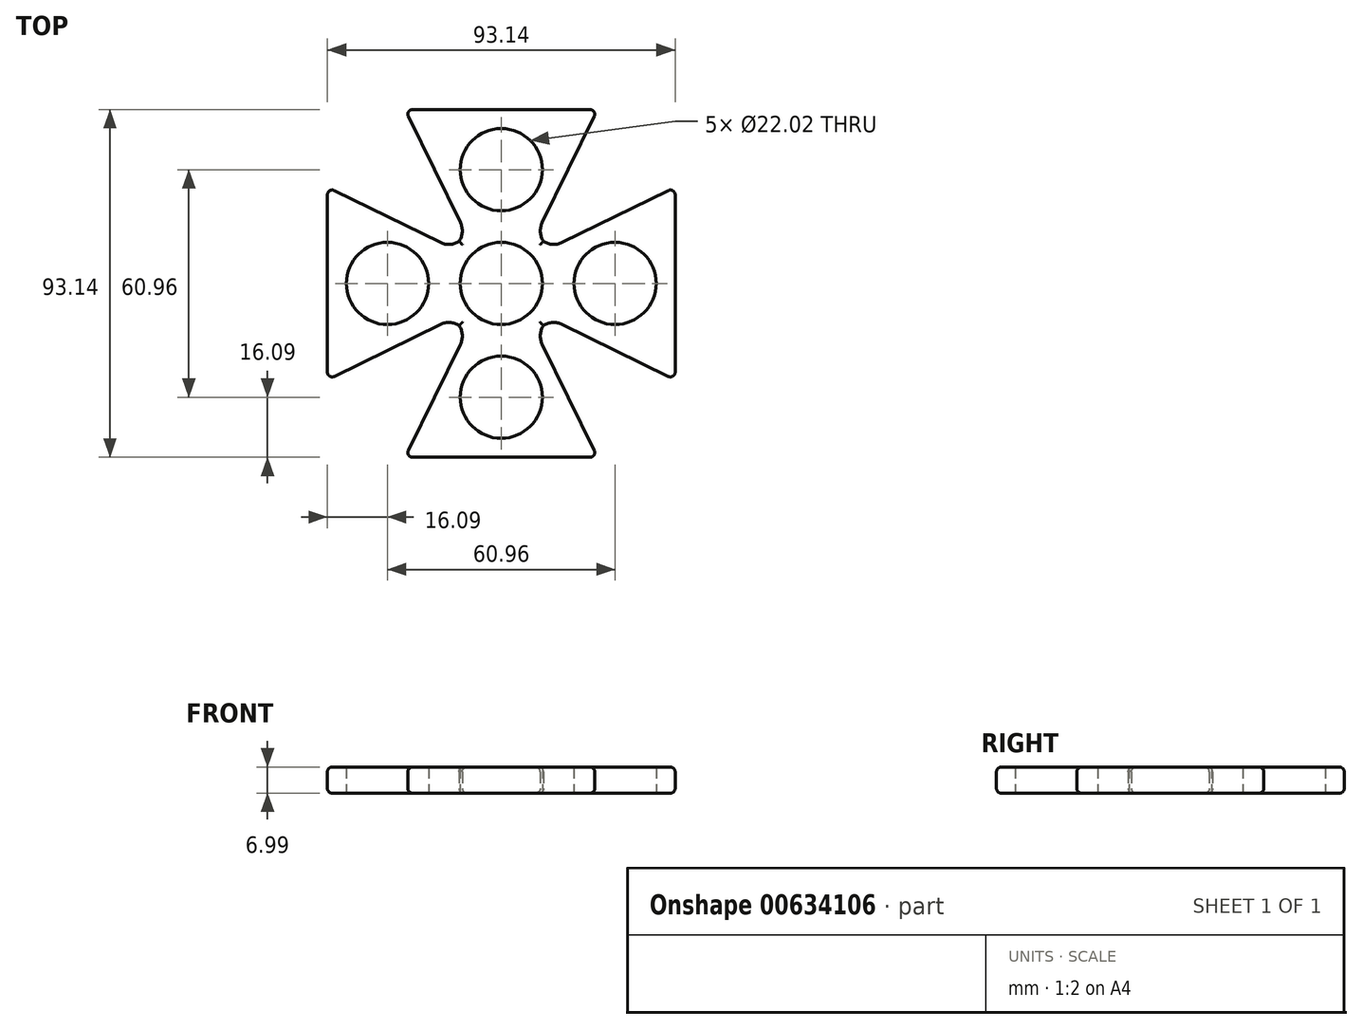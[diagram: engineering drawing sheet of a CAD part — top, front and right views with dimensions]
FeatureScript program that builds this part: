
annotation { "Feature Type Name" : "Feature", "Feature Type Description" : "" }
export const myFeature = defineFeature(function(context is Context, id is Id, definition is map)
    precondition{}
    {
        {
            var Q0;
            Q0=qCreatedBy(makeId("Top.planeOp"),FACE);
            var sketch = newSketch(context, id + "F0", { "sketchPlane" : qUnion([Q0])});
            skCircle(sketch, "E0", {"center": v(0, 0) * mm, "radius": 11.01 * mm});
            skLineSegment(sketch, "E1", {"start": v(0, 0) * mm, "end": v(0, 30.48) * mm});
            skCircle(sketch, "E2", {"center": v(0, 30.48) * mm, "radius": 11.01 * mm});
            skCircle(sketch, "E3", {"center": v(0, 0) * mm, "radius": 15.88 * mm});
            skLineSegment(sketch, "E4", {"start": v(-9.3, 12.87) * mm, "end": v(-25.8, 46.57) * mm});
            skLineSegment(sketch, "E5", {"start": v(-25.8, 46.57) * mm, "end": v(25.8, 46.57) * mm});
            skLineSegment(sketch, "E6", {"start": v(25.8, 46.57) * mm, "end": v(9.3, 12.87) * mm});
            skLineSegment(sketch, "E7.1.0", {"start": v(-46.57, -25.8) * mm, "end": v(-46.57, 25.8) * mm});
            skLineSegment(sketch, "E7.1.1", {"start": v(-12.87, -9.3) * mm, "end": v(-46.57, -25.8) * mm});
            skCircle(sketch, "E7.1.2", {"center": v(-30.48, 0) * mm, "radius": 11.01 * mm});
            skLineSegment(sketch, "E7.1.3", {"start": v(-46.57, 25.8) * mm, "end": v(-12.87, 9.3) * mm});
            skLineSegment(sketch, "E7.1.4", {"start": v(0, 0) * mm, "end": v(-30.48, 0) * mm});
            skLineSegment(sketch, "E7.2.0", {"start": v(25.8, -46.57) * mm, "end": v(-25.8, -46.57) * mm});
            skLineSegment(sketch, "E7.2.1", {"start": v(9.3, -12.87) * mm, "end": v(25.8, -46.57) * mm});
            skCircle(sketch, "E7.2.2", {"center": v(0, -30.48) * mm, "radius": 11.01 * mm});
            skLineSegment(sketch, "E7.2.3", {"start": v(-25.8, -46.57) * mm, "end": v(-9.3, -12.87) * mm});
            skLineSegment(sketch, "E7.2.4", {"start": v(0, 0) * mm, "end": v(0, -30.48) * mm});
            skLineSegment(sketch, "E7.3.0", {"start": v(46.57, 25.8) * mm, "end": v(46.57, -25.8) * mm});
            skLineSegment(sketch, "E7.3.1", {"start": v(12.87, 9.3) * mm, "end": v(46.57, 25.8) * mm});
            skCircle(sketch, "E7.3.2", {"center": v(30.48, 0) * mm, "radius": 11.01 * mm});
            skLineSegment(sketch, "E7.3.3", {"start": v(46.57, -25.8) * mm, "end": v(12.87, -9.3) * mm});
            skLineSegment(sketch, "E7.3.4", {"start": v(0, 0) * mm, "end": v(30.48, 0) * mm});
            skPoint(sketch, "E8", {"position": v(0, 46.57) * mm});
            skLineSegment(sketch, "E9", {"start": v(0, 30.48) * mm, "end": v(0, 46.57) * mm});
            skLineSegment(sketch, "E10", {"start": v(0, 0) * mm, "end": v(-11.23, -11.23) * mm});
            skSolve(sketch);
        }
        {
            var Q0;
            Q0 = qSketchRegion(id + "F0", true);
            extrude(context, id + "F1", {"entities" : qUnion([Q0]), "depth" : 7 * mm, "offsetDistance" : 25.4 * mm});
        }
        {
            var Q0;
            Q0=makeQuery(id+"F1.opExtrude","SWEPT_EDGE",EDGE,{"disambiguationData":[OSD([sQuery(id+"F0.wireOp",EDGE,"E4"),sQuery(id+"F0.wireOp",EDGE,"E5")])]});
            var Q1;
            Q1=makeQuery(id+"F1.opExtrude","SWEPT_EDGE",EDGE,{"disambiguationData":[OSD([sQuery(id+"F0.wireOp",EDGE,"E7.1.0"),sQuery(id+"F0.wireOp",EDGE,"E7.1.3")])]});
            var Q2;
            Q2=makeQuery(id+"F1.opExtrude","SWEPT_EDGE",EDGE,{"disambiguationData":[OSD([sQuery(id+"F0.wireOp",EDGE,"E5"),sQuery(id+"F0.wireOp",EDGE,"E6")])]});
            var Q3;
            Q3=makeQuery(id+"F1.opExtrude","SWEPT_EDGE",EDGE,{"disambiguationData":[OSD([sQuery(id+"F0.wireOp",EDGE,"E7.3.0"),sQuery(id+"F0.wireOp",EDGE,"E7.3.1")])]});
            var Q4;
            Q4=makeQuery(id+"F1.opExtrude","SWEPT_EDGE",EDGE,{"disambiguationData":[OSD([sQuery(id+"F0.wireOp",EDGE,"E7.1.0"),sQuery(id+"F0.wireOp",EDGE,"E7.1.1")])]});
            var Q5;
            Q5=makeQuery(id+"F1.opExtrude","SWEPT_EDGE",EDGE,{"disambiguationData":[OSD([sQuery(id+"F0.wireOp",EDGE,"E7.2.0"),sQuery(id+"F0.wireOp",EDGE,"E7.2.3")])]});
            var Q6;
            Q6=makeQuery(id+"F1.opExtrude","SWEPT_EDGE",EDGE,{"disambiguationData":[OSD([sQuery(id+"F0.wireOp",EDGE,"E7.2.0"),sQuery(id+"F0.wireOp",EDGE,"E7.2.1")])]});
            var Q7;
            Q7=makeQuery(id+"F1.opExtrude","SWEPT_EDGE",EDGE,{"disambiguationData":[OSD([sQuery(id+"F0.wireOp",EDGE,"E7.3.0"),sQuery(id+"F0.wireOp",EDGE,"E7.3.3")])]});
            fillet(context, id + "F2", {"entities" : qUnion([Q0, Q1, Q2, Q3, Q4, Q5, Q6, Q7]), "radius" : 1.27 * mm, "tangentPropagation" : true, "allowEdgeOverflow" : false});
        }
        {
            var Q0;
            Q0=makeQuery(id+"F1.opExtrude","SWEPT_EDGE",EDGE,{"disambiguationData":[OSD([sQuery(id+"F0.wireOp",EDGE,"E3"),sQuery(id+"F0.wireOp",EDGE,"E6")])]});
            var Q1;
            Q1=makeQuery(id+"F1.opExtrude","SWEPT_EDGE",EDGE,{"disambiguationData":[OSD([sQuery(id+"F0.wireOp",EDGE,"E3"),sQuery(id+"F0.wireOp",EDGE,"E7.3.1")])]});
            var Q2;
            Q2=makeQuery(id+"F1.opExtrude","SWEPT_EDGE",EDGE,{"disambiguationData":[OSD([sQuery(id+"F0.wireOp",EDGE,"E3"),sQuery(id+"F0.wireOp",EDGE,"E7.3.3")])]});
            var Q3;
            Q3=makeQuery(id+"F1.opExtrude","SWEPT_EDGE",EDGE,{"disambiguationData":[OSD([sQuery(id+"F0.wireOp",EDGE,"E3"),sQuery(id+"F0.wireOp",EDGE,"E7.2.1")])]});
            var Q4;
            Q4=makeQuery(id+"F1.opExtrude","SWEPT_EDGE",EDGE,{"disambiguationData":[OSD([sQuery(id+"F0.wireOp",EDGE,"E3"),sQuery(id+"F0.wireOp",EDGE,"E7.2.3")])]});
            var Q5;
            Q5=makeQuery(id+"F1.opExtrude","SWEPT_EDGE",EDGE,{"disambiguationData":[OSD([sQuery(id+"F0.wireOp",EDGE,"E3"),sQuery(id+"F0.wireOp",EDGE,"E7.1.1")])]});
            var Q6;
            Q6=makeQuery(id+"F1.opExtrude","SWEPT_EDGE",EDGE,{"disambiguationData":[OSD([sQuery(id+"F0.wireOp",EDGE,"E3"),sQuery(id+"F0.wireOp",EDGE,"E7.1.3")])]});
            var Q7;
            Q7=makeQuery(id+"F1.opExtrude","SWEPT_EDGE",EDGE,{"disambiguationData":[OSD([sQuery(id+"F0.wireOp",EDGE,"E3"),sQuery(id+"F0.wireOp",EDGE,"E4")])]});
            fillet(context, id + "F3", {"entities" : qUnion([Q0, Q1, Q2, Q3, Q4, Q5, Q6, Q7]), "radius" : 5.08 * mm, "tangentPropagation" : true, "allowEdgeOverflow" : false});
        }
        {
            var Q0;
            Q0=makeQuery(id+"F1.opExtrude","CAP_EDGE",EDGE,{"disambiguationData":[OSD([sQuery(id+"F0.wireOp",EDGE,"E7.2.0")])],"isStart":true});
            var Q1;
            Q1=makeQuery(id+"F1.opExtrude","CAP_EDGE",EDGE,{"disambiguationData":[OSD([sQuery(id+"F0.wireOp",EDGE,"E7.1.3")])],"isStart":true});
            var Q2;
            Q2=makeQuery(id+"F1.opExtrude","CAP_EDGE",EDGE,{"disambiguationData":[OSD([sQuery(id+"F0.wireOp",EDGE,"E4")])],"isStart":true});
            var Q3;
            Q3=makeQuery(id+"F1.opExtrude","CAP_EDGE",EDGE,{"disambiguationData":[OSD([sQuery(id+"F0.wireOp",EDGE,"E7.3.1")])],"isStart":true});
            fillet(context, id + "F4", {"entities" : qUnion([Q0, Q1, Q2, Q3]), "radius" : 1.27 * mm, "tangentPropagation" : true, "allowEdgeOverflow" : false});
        }
        {
            var Q0;
            Q0=makeQuery(id+"F1.opExtrude","CAP_EDGE",EDGE,{"disambiguationData":[OSD([sQuery(id+"F0.wireOp",EDGE,"E7.2.1")])],"isStart":false});
            var Q1;
            Q1=makeQuery(id+"F1.opExtrude","CAP_EDGE",EDGE,{"disambiguationData":[OSD([sQuery(id+"F0.wireOp",EDGE,"E7.3.3")])],"isStart":false});
            var Q2;
            Q2=makeQuery(id+"F1.opExtrude","CAP_EDGE",EDGE,{"disambiguationData":[OSD([sQuery(id+"F0.wireOp",EDGE,"E6")])],"isStart":false});
            var Q3;
            Q3=makeQuery(id+"F1.opExtrude","CAP_EDGE",EDGE,{"disambiguationData":[OSD([sQuery(id+"F0.wireOp",EDGE,"E7.1.3")])],"isStart":false});
            fillet(context, id + "F5", {"entities" : qUnion([Q0, Q1, Q2, Q3]), "radius" : 1.27 * mm, "tangentPropagation" : true, "allowEdgeOverflow" : false});
        }
    });
